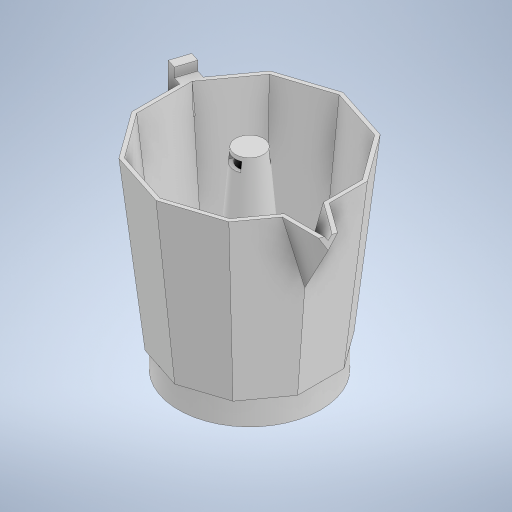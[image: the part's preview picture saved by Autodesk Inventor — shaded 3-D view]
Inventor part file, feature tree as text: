
AUTODESK INVENTOR PART (.ipt)
format: ipt  version: 2024 (Build 280153000, 153)  size: 827,904 bytes
history: native  units: mm
features: sketch x16, plane x5, extrude x5, loft x3, shell x2, hole x1, pattern_linear x1, projected_geometry x1
ambient origin geometry x8: Origin, YZ Plane, XZ Plane, XY Plane, X Axis, Y Axis, Z Axis, Center Point
bodies: Solid1 (feature_tree)
feature tree (34):
  sketch  "Sketch1"  dims[d1=80.0mm d2=23.51141mm]
  plane  "Work Plane1"
  loft  "Loft1"
  sketch  "Sketch3"  dims[d6=0.0mm d7=90.0deg d8=0.0mm d9=90.0deg]
  plane  "Work Plane2"
  sketch  "Sketch5"  dims[d14=0.0mm d15=75.0deg d16=75.0deg]
  plane  "Work Plane3"
  loft  "Loft2"
  shell  "Shell1"  Thickness=29.389263mm
  plane  "Work Plane4"
  extrude  "Extrusion1"  TaperAngle=0.0deg  [1 undecoded]
  loft  "Loft3"
  shell  "Shell2"  Thickness=75.0deg
  sketch  "Sketch10"  dims[d25=0.0mm d26=90.0deg]
  sketch  "Sketch11"  dims[d27=0.0mm d28=90.0deg]
  sketch  "Sketch12"  dims[d29=2.0mm]
  plane  "Work Plane13"
  extrude  "Extrusion2"  Depth=24.0mm
  extrude  "Extrusion3"  TaperAngle=60.0deg  [1 undecoded]
  extrude  "Extrusion4"  TaperAngle=0.0deg  [1 undecoded]
  hole  "Hole1"  [1 undecoded]
  pattern_linear  "Rectangular Pattern1"  Spacing1=0.0mm  [1 undecoded]
  extrude  "Extrusion5"  Depth=2.0mm
  sketch  "Sketch2"  dims[d3=90.0mm d4=100.0mm d5=29.389263mm]
  sketch  "Sketch6"  dims[d17=0.0mm d18=24.0mm]
  sketch  "Sketch7"  dims[d19=-25.0mm d20=60.0deg]
  sketch  "Sketch8"  dims[d21=60.0deg d22=0.0mm]
  sketch  "Sketch9"  dims[d23=0.0mm d24=8.0mm]
  sketch  "Sketch13"  dims[d30=-75.0mm]
  sketch  "Sketch15"  dims[d31=2.0mm d32=0.0mm]
  sketch  "Sketch16"  dims[d33=27.0mm]
  sketch  "Sketch17"  dims[d34=15.0mm]
  sketch  "Sketch18"  dims[d35=0.0mm d36=90.0deg d37=0.0mm d38=90.0deg d39=2.0mm d40=5.0mm d41=10.0mm d42=2.0mm d43=20.0mm d44=0.0mm d47=76.0mm d48=70.0mm d49=13.0mm d50=0.0mm d51=70.0mm d52=2.0mm d53=0.0mm d54=22.0mm d55=22.0mm d56=1.0mm d57=6.0mm d58=4.0mm d59=2.0mm d60=90.0deg d61=2.0mm d62=20.594885mm d63=230.0mm d65=2.0mm d66=230.0mm d68=2.0mm d69=5.0mm d70=5.0mm d71=5.0mm d72=20.0mm d73=10.0mm d74=0.0mm]
  projected_geometry  "Project Cut Edges1"
note: 5 required parameter values undecoded (feature->parameter linkage not recoverable at this tier; creation-order binding heuristic only, values carry confidence <= 0.55)
